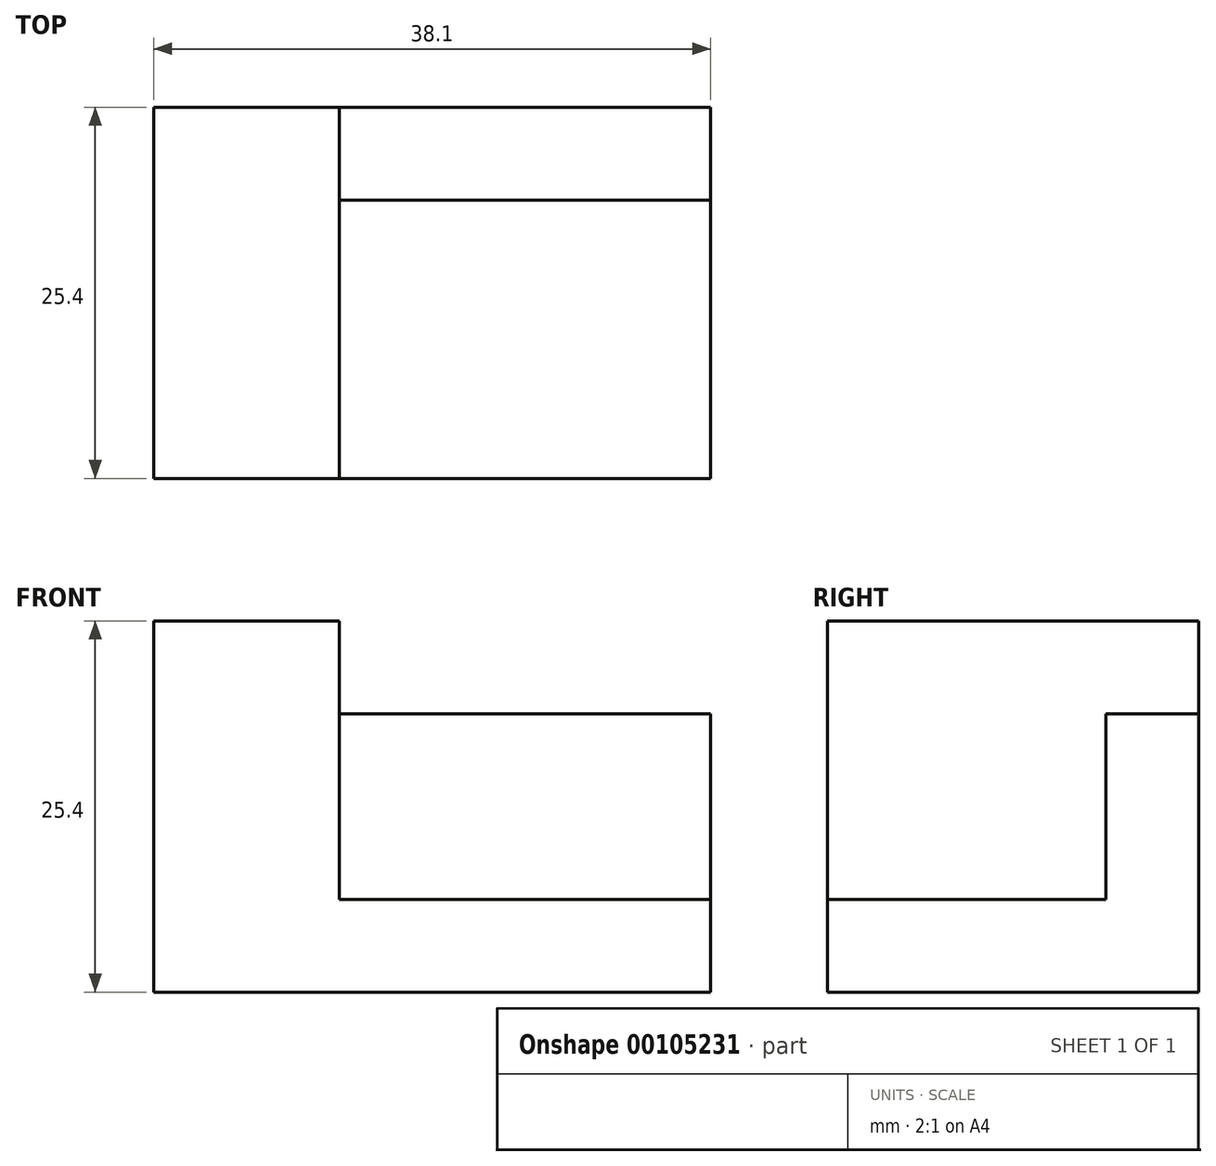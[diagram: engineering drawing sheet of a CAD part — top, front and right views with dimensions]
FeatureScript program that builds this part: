
annotation { "Feature Type Name" : "Feature", "Feature Type Description" : "" }
export const myFeature = defineFeature(function(context is Context, id is Id, definition is map)
    precondition{}
    {
        {
            var Q0;
            Q0=qCreatedBy(makeId("Front.planeOp"),FACE);
            var sketch = newSketch(context, id + "F0", { "sketchPlane" : qUnion([Q0])});
            skLineSegment(sketch, "E0.bottom", {"start": v(0, 0) * mm, "end": v(-38.1, 0) * mm});
            skLineSegment(sketch, "E0.top", {"start": v(0, 25.4) * mm, "end": v(-38.1, 25.4) * mm});
            skLineSegment(sketch, "E0.left", {"start": v(0, 0) * mm, "end": v(0, 25.4) * mm});
            skLineSegment(sketch, "E0.right", {"start": v(-38.1, 0) * mm, "end": v(-38.1, 25.4) * mm});
            skSolve(sketch);
        }
        {
            var Q0;
            Q0 = qSketchRegion(id + "F0", true);
            extrude(context, id + "F1", {"entities" : qUnion([Q0]), "endBound" : BoundingType.SYMMETRIC, "depth" : 25.4 * mm});
        }
        {
            var Q0;
            Q0=qCreatedBy(makeId("Front.planeOp"),FACE);
            var sketch = newSketch(context, id + "F2", { "sketchPlane" : qUnion([Q0])});
            skLineSegment(sketch, "E1.bottom", {"start": v(-25.4, 25.4) * mm, "end": v(0, 25.4) * mm});
            skLineSegment(sketch, "E1.top", {"start": v(-25.4, 19.05) * mm, "end": v(0, 19.05) * mm});
            skLineSegment(sketch, "E1.left", {"start": v(-25.4, 25.4) * mm, "end": v(-25.4, 19.05) * mm});
            skLineSegment(sketch, "E1.right", {"start": v(0, 25.4) * mm, "end": v(0, 19.05) * mm});
            skSolve(sketch);
        }
        {
            var Q0;
            Q0 = qSketchRegion(id + "F2", true);
            extrude(context, id + "F3", {"entities" : qUnion([Q0]), "operationType" : NewBodyOperationType.REMOVE, "endBound" : BoundingType.SYMMETRIC, "oppositeDirection" : true, "depth" : 25.4 * mm});
        }
        {
            var Q0;
            Q0=qCreatedBy(makeId("Front.planeOp"),FACE);
            var sketch = newSketch(context, id + "F4", { "sketchPlane" : qUnion([Q0])});
            skLineSegment(sketch, "E2.bottom", {"start": v(-25.4, 19.05) * mm, "end": v(0, 19.05) * mm});
            skLineSegment(sketch, "E2.top", {"start": v(-25.4, 6.35) * mm, "end": v(0, 6.35) * mm});
            skLineSegment(sketch, "E2.left", {"start": v(-25.4, 19.05) * mm, "end": v(-25.4, 6.35) * mm});
            skLineSegment(sketch, "E2.right", {"start": v(0, 19.05) * mm, "end": v(0, 6.35) * mm});
            skSolve(sketch);
        }
        {
            var Q0;
            Q0 = qSketchRegion(id + "F4", true);
            extrude(context, id + "F5", {"entities" : qUnion([Q0]), "operationType" : NewBodyOperationType.REMOVE, "endBound" : BoundingType.UP_TO_NEXT, "depth" : 19.05 * mm, "hasSecondDirection" : true, "secondDirectionOppositeDirection" : true, "secondDirectionDepth" : 6.35 * mm});
        }
    });
